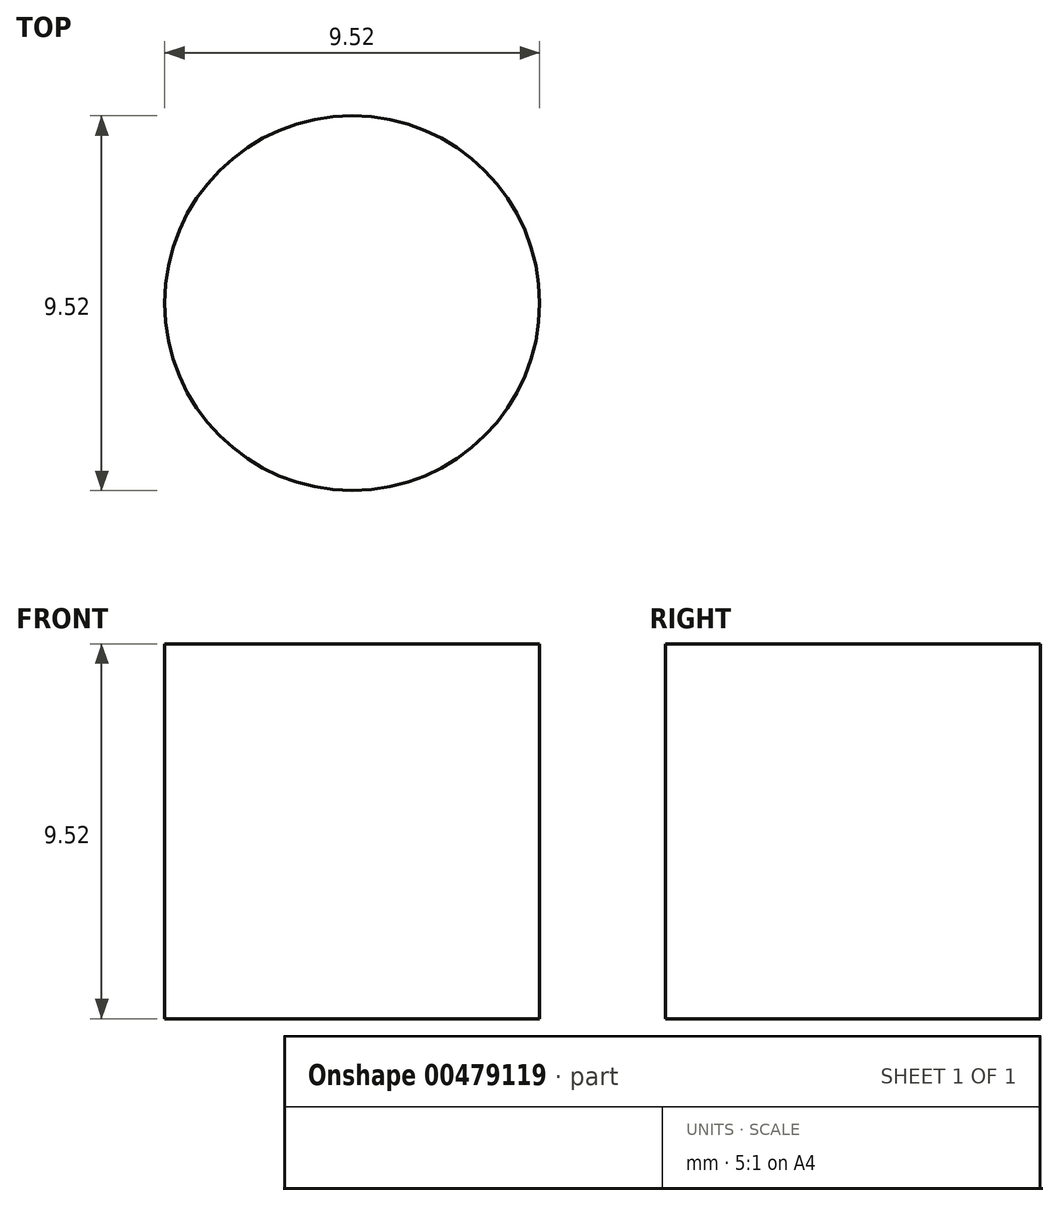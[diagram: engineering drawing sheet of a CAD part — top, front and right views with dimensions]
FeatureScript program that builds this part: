
annotation { "Feature Type Name" : "Feature", "Feature Type Description" : "" }
export const myFeature = defineFeature(function(context is Context, id is Id, definition is map)
    precondition{}
    {
        {
            var Q0;
            Q0=qCreatedBy(makeId("Top.planeOp"),FACE);
            var sketch = newSketch(context, id + "F0", { "sketchPlane" : qUnion([Q0])});
            skCircle(sketch, "E0", {"center": v(0, 0) * mm, "radius": 4.76 * mm});
            skSolve(sketch);
        }
        {
            var Q0;
            Q0=makeQuery(id+"F0.imprint","IMPRINT",FACE,{"disambiguationData":[TD([[makeQuery(id+"F0.imprint","IMPRINT",EDGE,{"derivedFrom":sQuery(id+"F0.wireOp",EDGE,"E0")}),1.0]])]});
            extrude(context, id + "F1", {"entities" : qUnion([Q0]), "endBound" : BoundingType.SYMMETRIC, "depth" : 9.52 * mm});
        }
    });
